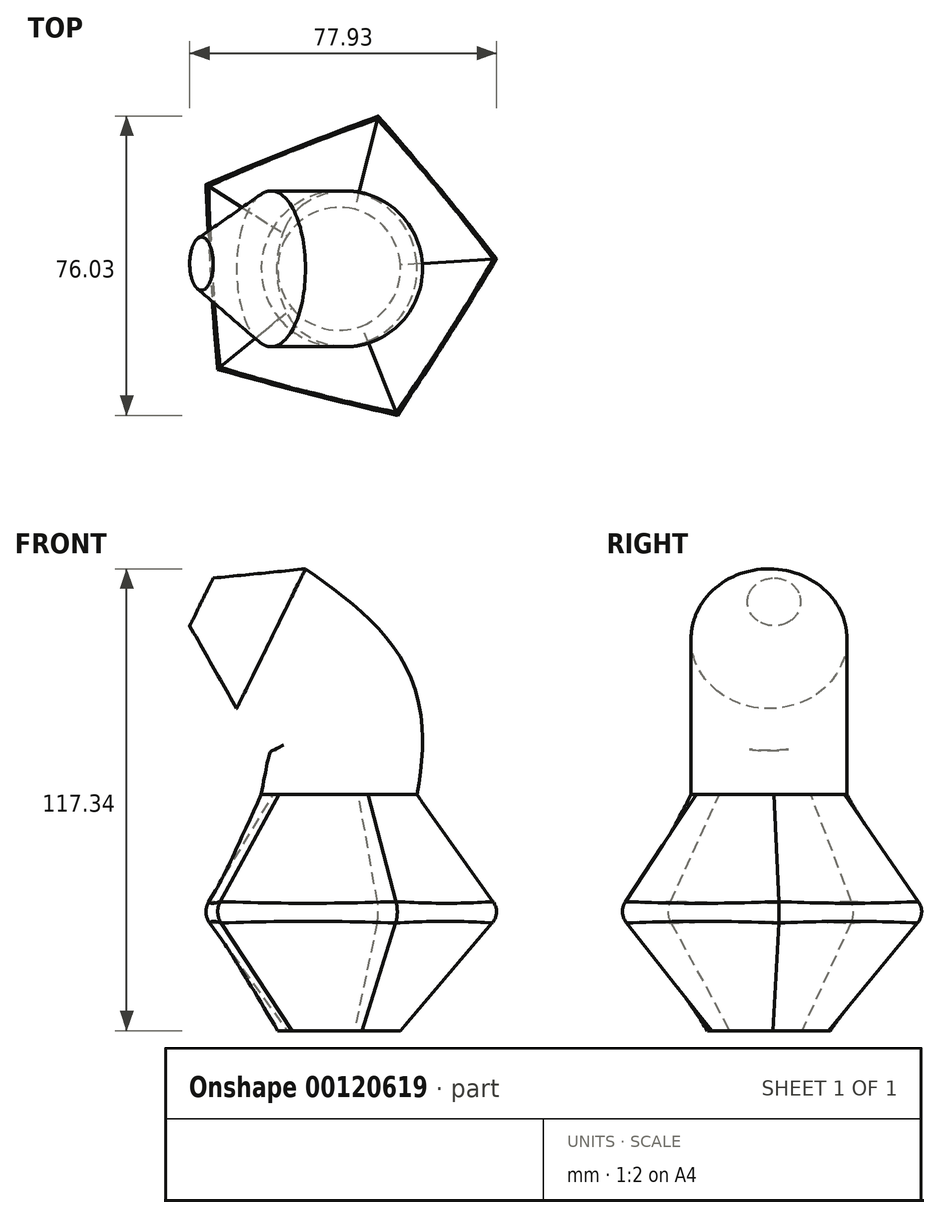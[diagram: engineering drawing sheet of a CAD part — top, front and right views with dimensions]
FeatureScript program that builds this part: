
annotation { "Feature Type Name" : "Feature", "Feature Type Description" : "" }
export const myFeature = defineFeature(function(context is Context, id is Id, definition is map)
    precondition{}
    {
        {
            var Q0;
            Q0=qCreatedBy(makeId("Top.planeOp"),FACE);
            var sketch = newSketch(context, id + "F0", { "sketchPlane" : qUnion([Q0])});
            skCircle(sketch, "E0", {"center": v(0, 0) * mm, "radius": 15.62 * mm});
            skSolve(sketch);
        }
        {
            var Q0;
            Q0=qCreatedBy(makeId("Top.planeOp"),FACE);
            cPlane(context, id + "F1", {"entities" : qUnion([Q0]), "cplaneType" : CPlaneType.OFFSET, "offset" : 30 * mm, "width" : 150 * mm, "height" : 150 * mm});
        }
        {
            var Q0;
            Q0=qCreatedBy(id+"F1.planeOp",FACE);
            var sketch = newSketch(context, id + "F2", { "sketchPlane" : qUnion([Q0])});
            skCircle(sketch, "E1.cCircle", {"center": v(0, 0) * mm, "radius": 33.33 * mm, "construction": true});
            skLineSegment(sketch, "E1.0", {"start": v(41.11, 2.62) * mm, "end": v(15.2, -38.29) * mm});
            skLineSegment(sketch, "E1.1", {"start": v(15.2, -38.29) * mm, "end": v(-31.72, -26.28) * mm});
            skLineSegment(sketch, "E1.2", {"start": v(-31.72, -26.28) * mm, "end": v(-34.8, 22.05) * mm});
            skLineSegment(sketch, "E1.3", {"start": v(-34.8, 22.05) * mm, "end": v(10.22, 39.9) * mm});
            skLineSegment(sketch, "E1.4", {"start": v(10.22, 39.9) * mm, "end": v(41.11, 2.62) * mm});
            skPoint(sketch, "E1.0.midPoint", {"position": v(28.15, -17.84) * mm});
            skSolve(sketch);
        }
        {
            var Q0;
            Q0=makeQuery(id+"F2.imprint","IMPRINT",FACE,{"disambiguationData":[TD([[makeQuery(id+"F2.imprint","IMPRINT",EDGE,{"derivedFrom":sQuery(id+"F2.wireOp",EDGE,"E1.0")}),-1.0]])]});
            var Q1;
            Q1=makeQuery(id+"F0.imprint","IMPRINT",FACE,{"disambiguationData":[TD([[makeQuery(id+"F0.imprint","IMPRINT",EDGE,{"derivedFrom":sQuery(id+"F0.wireOp",EDGE,"E0")}),1.0]])]});
            loft(context, id + "F3", {"sheetProfilesArray" : [{ "sheetProfileEntities" : qUnion([Q0]) }, { "sheetProfileEntities" : qUnion([Q1]) }]});
        }
        {
            var Q0;
            Q0=qCreatedBy(id+"F1.planeOp",FACE);
            cPlane(context, id + "F4", {"entities" : qUnion([Q0]), "cplaneType" : CPlaneType.OFFSET, "offset" : 30 * mm, "width" : 150 * mm, "height" : 150 * mm});
        }
        {
            var Q0;
            Q0=qCreatedBy(id+"F4.planeOp",FACE);
            var sketch = newSketch(context, id + "F5", { "sketchPlane" : qUnion([Q0])});
            skCircle(sketch, "E2", {"center": v(0, 0) * mm, "radius": 19.8 * mm});
            skSolve(sketch);
        }
        {
            var Q1;
            Q1=makeQuery(id+"F3.opLoft","CAP_FACE",FACE,{"disambiguationData":[OSD([makeQuery(id+"F2.imprint","IMPRINT",FACE,{"disambiguationData":[TD([[makeQuery(id+"F2.imprint","IMPRINT",EDGE,{"derivedFrom":sQuery(id+"F2.wireOp",EDGE,"E1.0")}),-1.0]])]})])],"isStart":true});
            var Q2;
            Q2=makeQuery(id+"F5.imprint","IMPRINT",FACE,{"disambiguationData":[TD([[makeQuery(id+"F5.imprint","IMPRINT",EDGE,{"derivedFrom":sQuery(id+"F5.wireOp",EDGE,"E2")}),1.0]])]});
            loft(context, id + "F6", {"operationType" : NewBodyOperationType.ADD, "sheetProfilesArray" : [{ "sheetProfileEntities" : qUnion([Q1]) }, { "sheetProfileEntities" : qUnion([Q2]) }]});
        }
        {
            var Q0;
            Q0=qCreatedBy(makeId("Front.planeOp"),FACE);
            var sketch = newSketch(context, id + "F7", { "sketchPlane" : qUnion([Q0])});
            skFitSpline(sketch, "E3", {"points": [v(0, 60.44) * mm, v(0, 82.12) * mm, v(-17.7, 99.78) * mm], "startDerivative": vector(8.24, 47.57) * mm, "endDerivative": vector(-43.02, 31.3) * mm});
            skSolve(sketch);
        }
        {
            var Q0;
            Q0=makeQuery(id+"F6.opLoft","CAP_FACE",FACE,{"disambiguationData":[OSD([makeQuery(id+"F5.imprint","IMPRINT",FACE,{"disambiguationData":[TD([[makeQuery(id+"F5.imprint","IMPRINT",EDGE,{"derivedFrom":sQuery(id+"F5.wireOp",EDGE,"E2")}),1.0]])]})])],"isStart":true});
            var Q1;
            Q1=sQuery(id+"F7.wireOp",EDGE,"E3");
            sweep(context, id + "F8", {"operationType" : NewBodyOperationType.ADD, "profiles" : qUnion([Q0]), "path" : qUnion([Q1])});
        }
        {
            var Q0;
            Q0=makeQuery(id+"F8.opSweep","CAP_FACE",FACE,{"disambiguationData":[OSD([makeQuery(id+"F5.imprint","IMPRINT",FACE,{"disambiguationData":[TD([[makeQuery(id+"F5.imprint","IMPRINT",EDGE,{"derivedFrom":sQuery(id+"F5.wireOp",EDGE,"E2")}),1.0]])]}),sQuery(id+"F7.wireOp",VERTEX,"E3.end")])],"isStart":false});
            cPlane(context, id + "F9", {"entities" : qUnion([Q0]), "cplaneType" : CPlaneType.OFFSET, "offset" : 20 * mm, "width" : 150 * mm, "height" : 150 * mm});
        }
        {
            var Q0;
            Q0=qCreatedBy(id+"F9.planeOp",FACE);
            var sketch = newSketch(context, id + "F10", { "sketchPlane" : qUnion([Q0])});
            skCircle(sketch, "E4", {"center": v(-1.3, 82.29) * mm, "radius": 6.75 * mm});
            skSolve(sketch);
        }
        {
            var Q1;
            Q1=makeQuery(id+"F10.imprint","IMPRINT",FACE,{"disambiguationData":[TD([[makeQuery(id+"F10.imprint","IMPRINT",EDGE,{"derivedFrom":sQuery(id+"F10.wireOp",EDGE,"E4")}),1.0]])]});
            var Q2;
            Q2=makeQuery(id+"F8.opSweep","CAP_FACE",FACE,{"disambiguationData":[OSD([makeQuery(id+"F5.imprint","IMPRINT",FACE,{"disambiguationData":[TD([[makeQuery(id+"F5.imprint","IMPRINT",EDGE,{"derivedFrom":sQuery(id+"F5.wireOp",EDGE,"E2")}),1.0]])]}),sQuery(id+"F7.wireOp",VERTEX,"E3.end")])],"isStart":false});
            loft(context, id + "F11", {"operationType" : NewBodyOperationType.ADD, "sheetProfilesArray" : [{ "sheetProfileEntities" : qUnion([Q1]) }, { "sheetProfileEntities" : qUnion([Q2]) }]});
        }
        {
            var Q0;
            {var subQ0=sQuery(id+"F2.wireOp",EDGE,"E1.4");var subQ1=sQuery(id+"F2.wireOp",EDGE,"E1.1");var subQ2=sQuery(id+"F2.wireOp",EDGE,"E1.0");Q0=makeQuery(id+"F6.boolean.opBoolean","MERGE",EDGE,{"derivedFrom":[makeQuery(id+"F3.opLoft","MID_CAP_EDGE",EDGE,{"disambiguationData":[OSD([subQ2,subQ1,subQ0])],"capPos":0.0}),makeQuery(id+"F6.opLoft","MID_CAP_EDGE",EDGE,{"disambiguationData":[OSD([subQ2,subQ1,subQ0])],"capPos":0.0})]});}
            var Q1;
            {var subQ0=sQuery(id+"F2.wireOp",EDGE,"E1.4");var subQ1=sQuery(id+"F2.wireOp",EDGE,"E1.3");var subQ2=sQuery(id+"F2.wireOp",EDGE,"E1.0");Q1=makeQuery(id+"F6.boolean.opBoolean","MERGE",EDGE,{"derivedFrom":[makeQuery(id+"F3.opLoft","MID_CAP_EDGE",EDGE,{"disambiguationData":[OSD([subQ2,subQ1,subQ0])],"capPos":0.0}),makeQuery(id+"F6.opLoft","MID_CAP_EDGE",EDGE,{"disambiguationData":[OSD([subQ2,subQ1,subQ0])],"capPos":0.0})]});}
            var Q2;
            {var subQ0=sQuery(id+"F2.wireOp",EDGE,"E1.4");var subQ1=sQuery(id+"F2.wireOp",EDGE,"E1.3");var subQ2=sQuery(id+"F2.wireOp",EDGE,"E1.2");Q2=makeQuery(id+"F6.boolean.opBoolean","MERGE",EDGE,{"derivedFrom":[makeQuery(id+"F3.opLoft","MID_CAP_EDGE",EDGE,{"disambiguationData":[OSD([subQ2,subQ1,subQ0])],"capPos":0.0}),makeQuery(id+"F6.opLoft","MID_CAP_EDGE",EDGE,{"disambiguationData":[OSD([subQ2,subQ1,subQ0])],"capPos":0.0})]});}
            var Q3;
            {var subQ0=sQuery(id+"F2.wireOp",EDGE,"E1.3");var subQ1=sQuery(id+"F2.wireOp",EDGE,"E1.2");var subQ2=sQuery(id+"F2.wireOp",EDGE,"E1.1");Q3=makeQuery(id+"F6.boolean.opBoolean","MERGE",EDGE,{"derivedFrom":[makeQuery(id+"F3.opLoft","MID_CAP_EDGE",EDGE,{"disambiguationData":[OSD([subQ2,subQ1,subQ0])],"capPos":0.0}),makeQuery(id+"F6.opLoft","MID_CAP_EDGE",EDGE,{"disambiguationData":[OSD([subQ2,subQ1,subQ0])],"capPos":0.0})]});}
            var Q4;
            {var subQ0=sQuery(id+"F2.wireOp",EDGE,"E1.2");var subQ1=sQuery(id+"F2.wireOp",EDGE,"E1.1");var subQ2=sQuery(id+"F2.wireOp",EDGE,"E1.0");Q4=makeQuery(id+"F6.boolean.opBoolean","MERGE",EDGE,{"derivedFrom":[makeQuery(id+"F3.opLoft","MID_CAP_EDGE",EDGE,{"disambiguationData":[OSD([subQ2,subQ1,subQ0])],"capPos":0.0}),makeQuery(id+"F6.opLoft","MID_CAP_EDGE",EDGE,{"disambiguationData":[OSD([subQ2,subQ1,subQ0])],"capPos":0.0})]});}
            fillet(context, id + "F12", {"entities" : qUnion([Q0, Q1, Q2, Q3, Q4]), "radius" : 5 * mm, "tangentPropagation" : true, "allowEdgeOverflow" : false});
        }
    });
